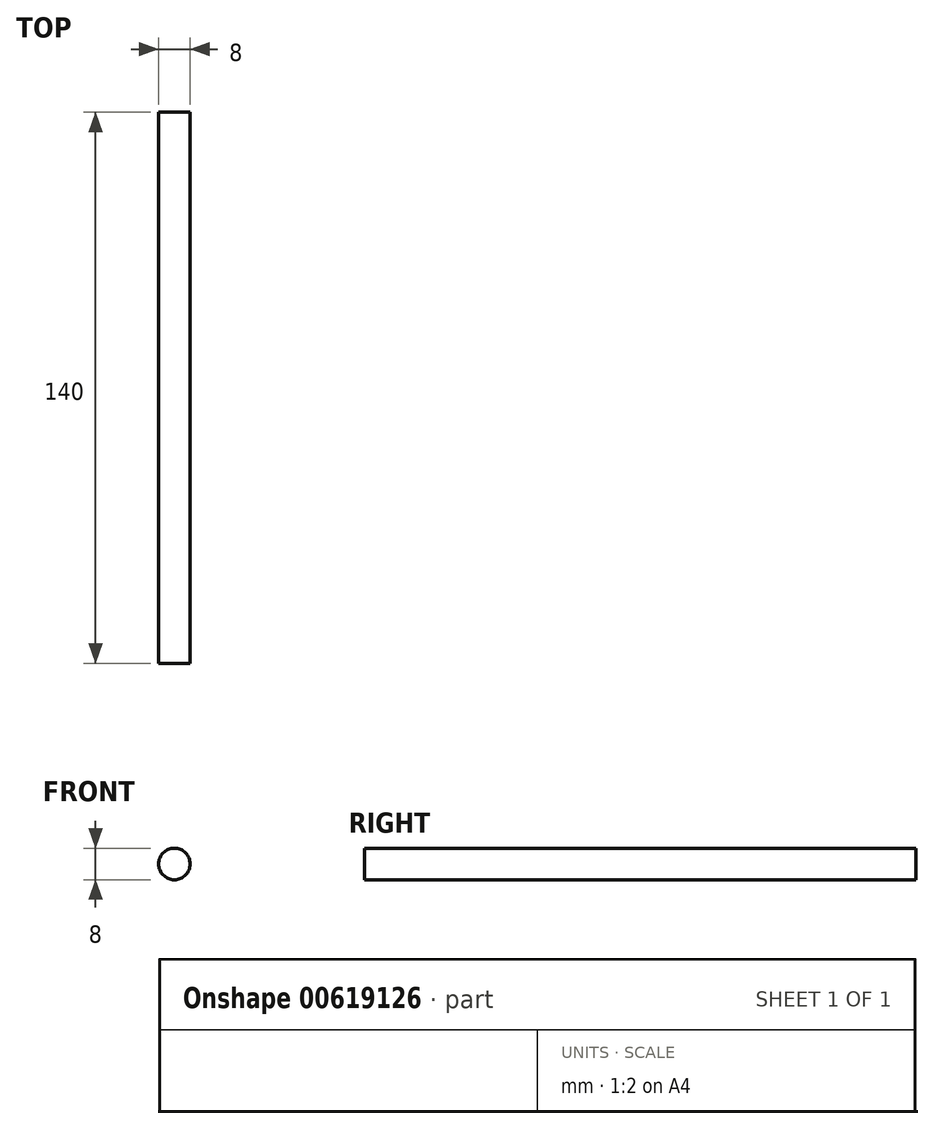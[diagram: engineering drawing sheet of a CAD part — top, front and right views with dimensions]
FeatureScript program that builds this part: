
annotation { "Feature Type Name" : "Feature", "Feature Type Description" : "" }
export const myFeature = defineFeature(function(context is Context, id is Id, definition is map)
    precondition{}
    {
        {
            var Q0;
            Q0=qCreatedBy(makeId("Front.planeOp"),FACE);
            var sketch = newSketch(context, id + "F0", { "sketchPlane" : qUnion([Q0])});
            skCircle(sketch, "E0", {"center": v(0, 0) * mm, "radius": 4 * mm});
            skSolve(sketch);
        }
        {
            var Q0;
            Q0=qSketchRegion(id+"F0",true);
            extrude(context, id + "F1", {"entities" : qUnion([Q0]), "depth" : 140 * mm, "offsetDistance" : 25 * mm});
        }
    });
